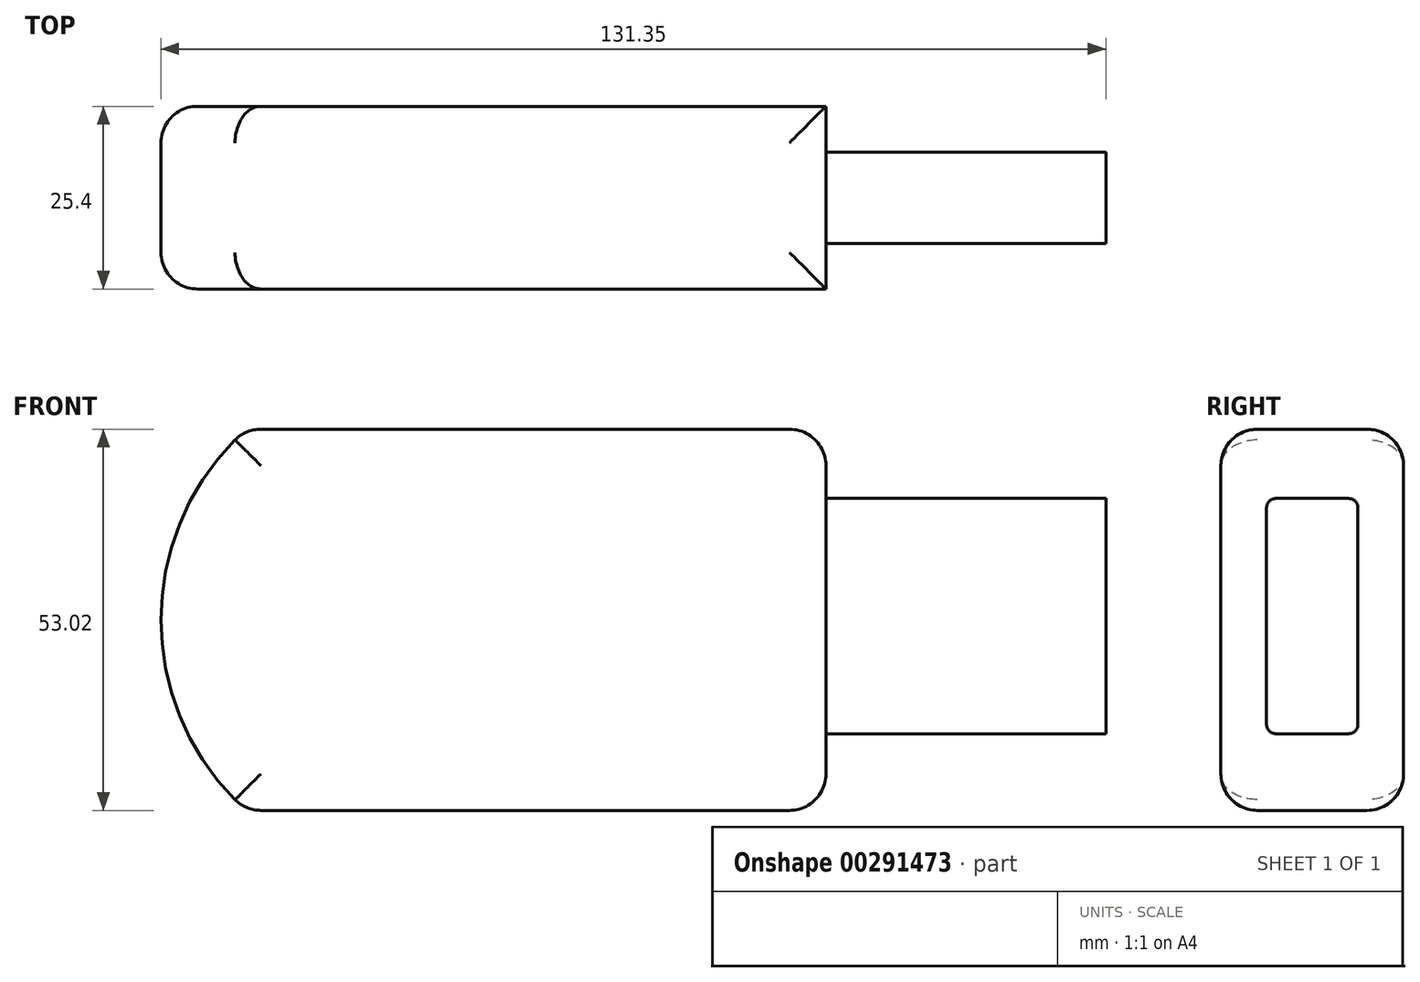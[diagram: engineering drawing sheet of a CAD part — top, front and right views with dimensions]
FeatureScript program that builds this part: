
annotation { "Feature Type Name" : "Feature", "Feature Type Description" : "" }
export const myFeature = defineFeature(function(context is Context, id is Id, definition is map)
    precondition{}
    {
        {
            var Q0;
            Q0=qCreatedBy(makeId("Front.planeOp"),FACE);
            var sketch = newSketch(context, id + "F0", { "sketchPlane" : qUnion([Q0])});
            skLineSegment(sketch, "E0.bottom", {"start": v(0, -3.44) * mm, "end": v(-80.56, -3.44) * mm});
            skLineSegment(sketch, "E0.top", {"start": v(0, 49.58) * mm, "end": v(-80.56, 49.58) * mm});
            skLineSegment(sketch, "E0.left", {"start": v(0, -3.44) * mm, "end": v(0, 49.58) * mm});
            skPoint(sketch, "E0.middle", {"position": v(-40.28, 23.07) * mm});
            skArc(sketch, "E1", {"start": v(-80.56, 49.58) * mm, "mid": v(-92.45, 23.07) * mm, "end": v(-80.56, -3.44) * mm});
            skSolve(sketch);
        }
        {
            var Q0;
            Q0=qCreatedBy(makeId("Front.planeOp"),FACE);
            var sketch = newSketch(context, id + "F1", { "sketchPlane" : qUnion([Q0])});
            skLineSegment(sketch, "E2.bottom", {"start": v(0, 39.94) * mm, "end": v(38.9, 39.94) * mm});
            skLineSegment(sketch, "E2.top", {"start": v(0, 7.23) * mm, "end": v(38.9, 7.23) * mm});
            skLineSegment(sketch, "E2.left", {"start": v(0, 39.94) * mm, "end": v(0, 7.23) * mm});
            skLineSegment(sketch, "E2.right", {"start": v(38.9, 39.94) * mm, "end": v(38.9, 7.23) * mm});
            skSolve(sketch);
        }
        {
            var Q0;
            Q0=makeQuery(id+"F0.imprint","IMPRINT",FACE,{"disambiguationData":[TD([[makeQuery(id+"F0.imprint","IMPRINT",EDGE,{"derivedFrom":sQuery(id+"F0.wireOp",EDGE,"E0.bottom")}),-1.0]])]});
            extrude(context, id + "F2", {"entities" : qUnion([Q0]), "endBound" : BoundingType.SYMMETRIC, "depth" : 25.4 * mm});
        }
        {
            var Q0;
            Q0=makeQuery(id+"F1.imprint","IMPRINT",FACE,{"disambiguationData":[TD([[makeQuery(id+"F1.imprint","IMPRINT",EDGE,{"derivedFrom":sQuery(id+"F1.wireOp",EDGE,"E2.bottom")}),-1.0]])]});
            extrude(context, id + "F3", {"entities" : qUnion([Q0]), "operationType" : NewBodyOperationType.ADD, "endBound" : BoundingType.SYMMETRIC, "depth" : 12.7 * mm});
        }
        {
            var Q0;
            Q0=makeQuery(id+"F2.opExtrude","CAP_EDGE",EDGE,{"disambiguationData":[OSD([sQuery(id+"F0.wireOp",EDGE,"E0.bottom")])],"isStart":false});
            var Q1;
            Q1=makeQuery(id+"F2.opExtrude","CAP_EDGE",EDGE,{"disambiguationData":[OSD([sQuery(id+"F0.wireOp",EDGE,"E0.top")])],"isStart":false});
            var Q2;
            Q2=makeQuery(id+"F2.opExtrude","CAP_EDGE",EDGE,{"disambiguationData":[OSD([sQuery(id+"F0.wireOp",EDGE,"E0.bottom")])],"isStart":true});
            var Q3;
            Q3=makeQuery(id+"F2.opExtrude","CAP_EDGE",EDGE,{"disambiguationData":[OSD([sQuery(id+"F0.wireOp",EDGE,"E0.top")])],"isStart":true});
            var Q4;
            Q4=makeQuery(id+"F2.opExtrude","CAP_EDGE",EDGE,{"disambiguationData":[OSD([sQuery(id+"F0.wireOp",EDGE,"E0.right")])],"isStart":true});
            var Q5;
            Q5=makeQuery(id+"F2.opExtrude","SWEPT_EDGE",EDGE,{"disambiguationData":[OSD([sQuery(id+"F0.wireOp",EDGE,"E0.top"),sQuery(id+"F0.wireOp",EDGE,"E0.right")])]});
            var Q6;
            Q6=makeQuery(id+"F2.opExtrude","CAP_EDGE",EDGE,{"disambiguationData":[OSD([sQuery(id+"F0.wireOp",EDGE,"E0.right")])],"isStart":false});
            var Q7;
            Q7=makeQuery(id+"F2.opExtrude","SWEPT_EDGE",EDGE,{"disambiguationData":[OSD([sQuery(id+"F0.wireOp",EDGE,"E0.bottom"),sQuery(id+"F0.wireOp",EDGE,"E0.right")])]});
            fillet(context, id + "F4", {"entities" : qUnion([Q0, Q1, Q2, Q3, Q4, Q5, Q6, Q7]), "radius" : 5.08 * mm, "tangentPropagation" : true, "allowEdgeOverflow" : false});
        }
        {
            var Q0;
            Q0=makeQuery(id+"F3.opExtrude","CAP_EDGE",EDGE,{"disambiguationData":[OSD([sQuery(id+"F1.wireOp",EDGE,"E2.bottom")])],"isStart":false});
            var Q1;
            Q1=makeQuery(id+"F3.opExtrude","CAP_EDGE",EDGE,{"disambiguationData":[OSD([sQuery(id+"F1.wireOp",EDGE,"E2.top")])],"isStart":false});
            var Q2;
            Q2=makeQuery(id+"F3.opExtrude","CAP_EDGE",EDGE,{"disambiguationData":[OSD([sQuery(id+"F1.wireOp",EDGE,"E2.bottom")])],"isStart":true});
            var Q3;
            Q3=makeQuery(id+"F3.opExtrude","CAP_EDGE",EDGE,{"disambiguationData":[OSD([sQuery(id+"F1.wireOp",EDGE,"E2.top")])],"isStart":true});
            fillet(context, id + "F5", {"entities" : qUnion([Q0, Q1, Q2, Q3]), "radius" : 1.27 * mm, "tangentPropagation" : true, "allowEdgeOverflow" : false});
        }
        {
            var Q0;
            Q0=makeQuery(id+"F2.opExtrude","CAP_EDGE",EDGE,{"disambiguationData":[OSD([sQuery(id+"F0.wireOp",EDGE,"E1")])],"isStart":true});
            var Q1;
            Q1=makeQuery(id+"F2.opExtrude","CAP_EDGE",EDGE,{"disambiguationData":[OSD([sQuery(id+"F0.wireOp",EDGE,"E1")])],"isStart":false});
            fillet(context, id + "F6", {"entities" : qUnion([Q0, Q1]), "radius" : 5.08 * mm, "tangentPropagation" : true, "allowEdgeOverflow" : false});
        }
    });
